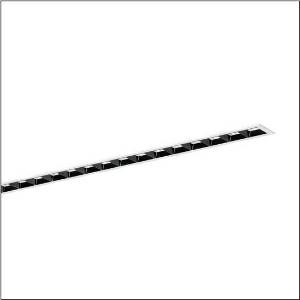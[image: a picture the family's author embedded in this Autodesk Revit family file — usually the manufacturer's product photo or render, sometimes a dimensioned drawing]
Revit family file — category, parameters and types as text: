
# Revit family: silica_r__21_51mx12dc3awb_9b9c
name_source: partatom
category: Lighting Fixtures
units: mm (PartAtom-declared; Revit-internal decimal feet)

## family parameters
Cut with Voids When Loaded = No
Host = Face
Light Source = No
Part Type = Normal
Room Calculation Point = No
Round Connector Dimension = Use Diameter
Shared = No

## types (1)
- --- (1 x LED, 10800 lm, 69.2 W, 3000K)
    Apparent Load = 69 VA
    CIE Flux Codes = 86 100 100 100 100
    Color Rendering = 80
    Color Temperature = 3000K
    Default Elevation = 1800 mm
    Description = Silica® 21, office luminaire, primary light control with darklight reflector, of PMMA, black, CAT 2 (L<= 3000cd/m²), light emission: direct distribution, primary light characteristic: symmetric, installation type: recessed, LED, rated luminous flux: 10.800lm, luminous efficacy: 156lm/W, light colour: 830, colour temperature: 3000K, with terminal, 3+2-pole, max. 2.5mm², mains connection: 220..240V, AC, 50/60Hz, rated input power: 69.2W, luminaire housing, of aluminium, traffic white (RAL 9016), length: 3.028mm, width: 79mm, height: 53mm, protection rating (complete): IP20, insulation class (complete): insulation class I (protective earthing), certification: CE, permissible operating ambient temperature: 0..+35°C, standard: EN 50419, packaging unit: 1 piece
    Height = 0 mm  [stored 0 ft]
    Lamp = 1 x LED
    Lamp Light Flux = 10800 lm
    Lamp Power = 69.2 W
    Lamp count = 1
    Length = 3027 mm
    Luminous efficacy = 156 lm/W
    Manufacturer = Siteco
    ModVariant = No
    Model = 51MX12DC3AWB
    Mounting Place = Ceiling
    Mounting Type = Recessed
    Number of Poles = 1
    OnlyDefault = Yes
    Power Factor = 1
    Product Name = Silica® 21
    Product group = office luminaire | ceiling recessed
    ProductGroupID = 400
    Protection Class = Protection class I
    Protection Degree = IP 20
    RLX_Detail_Level = 1
    RlxData = <blob elided: 63477 chars, md5=1c35449c>
    Socket = socket
    Standby Power = 0 W
    System Light Flux = 10800 lm
    System Power = 69 W
    Type Comments = factory setting: luminous flux: 100 % | dim-lin: 254 | 392 mA
    Type Image = l_1251632.jpg
    URL = http://relux.com
    VarID = @adj_034025
    Voltage = 0 V
    Weight = 0.00 kg
    Width = 79 mm

note: [stored X ft] marks values corroborated as IEEE doubles in the binary element streams (Revit-internal decimal feet)

## geometry (parser evidence)
native form markers: Blend x4, Sweep x10
no freeform markers — native parametric forms only
